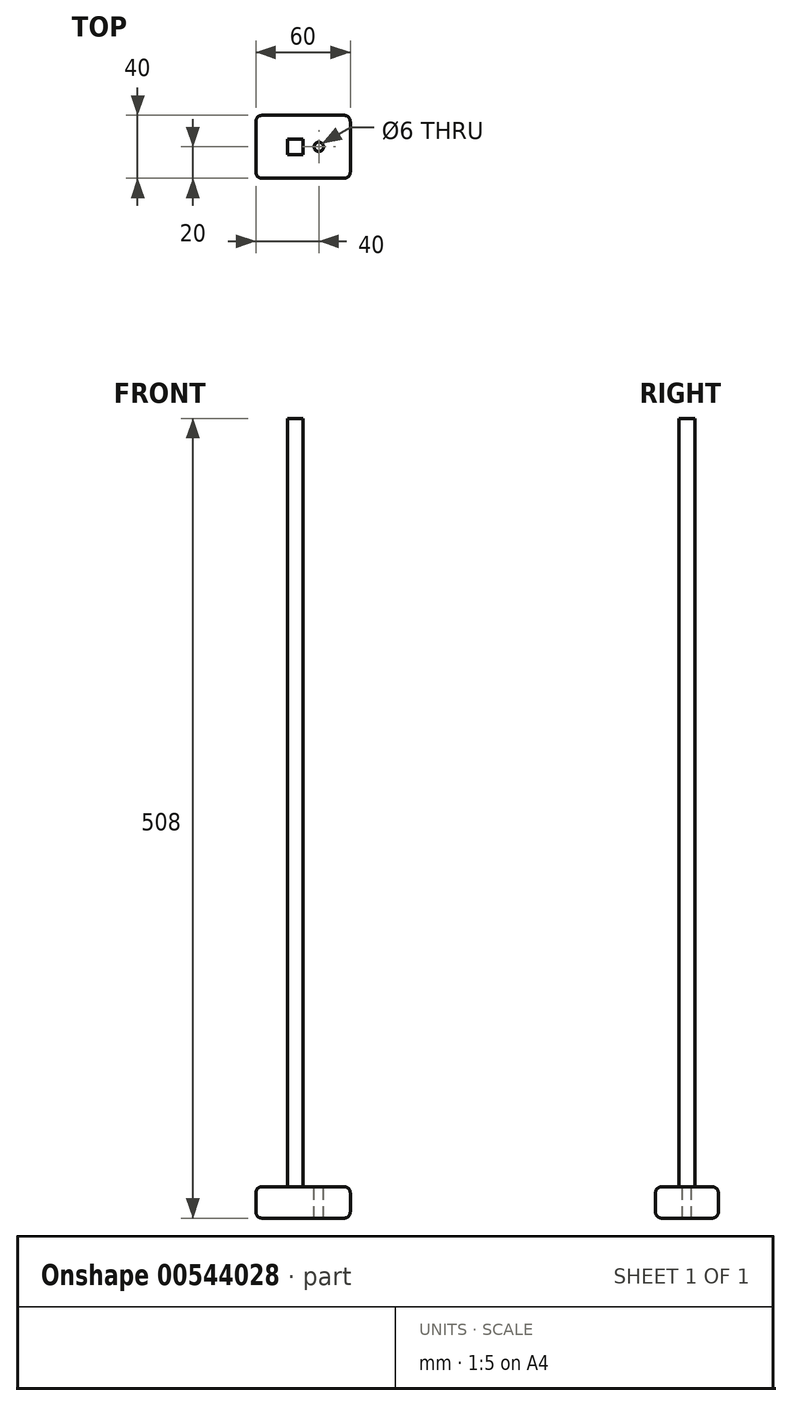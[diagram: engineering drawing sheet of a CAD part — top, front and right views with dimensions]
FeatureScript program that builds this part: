
annotation { "Feature Type Name" : "Feature", "Feature Type Description" : "" }
export const myFeature = defineFeature(function(context is Context, id is Id, definition is map)
    precondition{}
    {
        {
            var Q0;
            Q0=qCreatedBy(makeId("Front.planeOp"),FACE);
            var sketch = newSketch(context, id + "F0", { "sketchPlane" : qUnion([Q0])});
            skLineSegment(sketch, "E0.bottom", {"start": v(0, 0) * mm, "end": v(60, 0) * mm});
            skLineSegment(sketch, "E0.top", {"start": v(0, -20) * mm, "end": v(60, -20) * mm});
            skLineSegment(sketch, "E0.left", {"start": v(0, 0) * mm, "end": v(0, -20) * mm});
            skLineSegment(sketch, "E0.right", {"start": v(60, 0) * mm, "end": v(60, -20) * mm});
            skPoint(sketch, "E0.middle", {"position": v(30, -10) * mm});
            skSolve(sketch);
        }
        {
            var Q0;
            Q0=makeQuery(id+"F0.imprint","IMPRINT",FACE,{"disambiguationData":[TD([[makeQuery(id+"F0.imprint","IMPRINT",EDGE,{"derivedFrom":sQuery(id+"F0.wireOp",EDGE,"E0.bottom")}),-1.0]])]});
            extrude(context, id + "F1", {"entities" : qUnion([Q0]), "depth" : 40 * mm, "offsetDistance" : 25.4 * mm});
        }
        {
            var Q0;
            Q0=makeQuery(id+"F1.opExtrude","SWEPT_FACE",FACE,{"disambiguationData":[OSD([sQuery(id+"F0.wireOp",EDGE,"E0.bottom")])]});
            var sketch = newSketch(context, id + "F2", { "sketchPlane" : qUnion([Q0])});
            skCircle(sketch, "E1", {"center": v(40, -20) * mm, "radius": 10 * mm});
            skSolve(sketch);
        }
        {
            var Q0;
            Q0=makeQuery(id+"F1.opExtrude","CAP_EDGE",EDGE,{"disambiguationData":[OSD([sQuery(id+"F0.wireOp",EDGE,"E0.right")])],"isStart":true});
            var Q1;
            Q1=makeQuery(id+"F1.opExtrude","SWEPT_EDGE",EDGE,{"disambiguationData":[OSD([sQuery(id+"F0.wireOp",EDGE,"E0.top"),sQuery(id+"F0.wireOp",EDGE,"E0.left")])]});
            var Q2;
            Q2=makeQuery(id+"F1.opExtrude","CAP_EDGE",EDGE,{"disambiguationData":[OSD([sQuery(id+"F0.wireOp",EDGE,"E0.left")])],"isStart":true});
            var Q3;
            Q3=makeQuery(id+"F1.opExtrude","SWEPT_EDGE",EDGE,{"disambiguationData":[OSD([sQuery(id+"F0.wireOp",EDGE,"E0.bottom"),sQuery(id+"F0.wireOp",EDGE,"E0.left")])]});
            var Q4;
            Q4=makeQuery(id+"F1.opExtrude","CAP_EDGE",EDGE,{"disambiguationData":[OSD([sQuery(id+"F0.wireOp",EDGE,"E0.left")])],"isStart":false});
            var Q5;
            Q5=makeQuery(id+"F1.opExtrude","SWEPT_EDGE",EDGE,{"disambiguationData":[OSD([sQuery(id+"F0.wireOp",EDGE,"E0.top"),sQuery(id+"F0.wireOp",EDGE,"E0.right")])]});
            var Q6;
            Q6=makeQuery(id+"F1.opExtrude","CAP_EDGE",EDGE,{"disambiguationData":[OSD([sQuery(id+"F0.wireOp",EDGE,"E0.right")])],"isStart":false});
            var Q7;
            Q7=makeQuery(id+"F1.opExtrude","SWEPT_EDGE",EDGE,{"disambiguationData":[OSD([sQuery(id+"F0.wireOp",EDGE,"E0.bottom"),sQuery(id+"F0.wireOp",EDGE,"E0.right")])]});
            var Q8;
            Q8=makeQuery(id+"F1.opExtrude","CAP_EDGE",EDGE,{"disambiguationData":[OSD([sQuery(id+"F0.wireOp",EDGE,"E0.bottom")])],"isStart":false});
            var Q9;
            Q9=makeQuery(id+"F1.opExtrude","CAP_FACE",FACE,{"disambiguationData":[OSD([sQuery(id+"F0.wireOp",EDGE,"E0.bottom"),sQuery(id+"F0.wireOp",EDGE,"E0.top"),sQuery(id+"F0.wireOp",EDGE,"E0.left"),sQuery(id+"F0.wireOp",EDGE,"E0.right")])],"isStart":false});
            var Q10;
            Q10=makeQuery(id+"F1.opExtrude","CAP_EDGE",EDGE,{"disambiguationData":[OSD([sQuery(id+"F0.wireOp",EDGE,"E0.top")])],"isStart":true});
            var Q11;
            Q11=makeQuery(id+"F1.opExtrude","CAP_EDGE",EDGE,{"disambiguationData":[OSD([sQuery(id+"F0.wireOp",EDGE,"E0.bottom")])],"isStart":true});
            fillet(context, id + "F3", {"entities" : qUnion([Q0, Q1, Q2, Q3, Q4, Q5, Q6, Q7, Q8, Q9, Q10, Q11]), "radius" : 4 * mm, "tangentPropagation" : true, "allowEdgeOverflow" : false});
        }
        {
            var Q0;
            Q0=sQuery(id+"F2.wireOp",VERTEX,"E1.center");
            var Q1;
            Q1=makeQuery(id+"F1.opExtrude","SWEPT_BODY",BODY,{"disambiguationData":[OSD([sQuery(id+"F0.wireOp",EDGE,"E0.bottom"),sQuery(id+"F0.wireOp",EDGE,"E0.top"),sQuery(id+"F0.wireOp",EDGE,"E0.left"),sQuery(id+"F0.wireOp",EDGE,"E0.right")])]});
            hole(context, id + "F4", {"style" : HoleStyle.SIMPLE, "endStyle" : HoleEndStyle.THROUGH, "holeDiameter" : 6 * mm, "isTappedThrough" : true, "tappedDepth" : 12.7 * mm, "tapClearance" : 3, "locations" : qUnion([Q0]), "scope" : qUnion([Q1])});
        }
        {
            var Q0;
            Q0=makeQuery(id+"F1.opExtrude","SWEPT_FACE",FACE,{"disambiguationData":[OSD([sQuery(id+"F0.wireOp",EDGE,"E0.top")])]});
            var sketch = newSketch(context, id + "F5", { "sketchPlane" : qUnion([Q0])});
            skLineSegment(sketch, "E2.bottom", {"start": v(20, 25) * mm, "end": v(30, 25) * mm});
            skLineSegment(sketch, "E2.top", {"start": v(20, 15) * mm, "end": v(30, 15) * mm});
            skLineSegment(sketch, "E2.left", {"start": v(20, 25) * mm, "end": v(20, 15) * mm});
            skLineSegment(sketch, "E2.right", {"start": v(30, 25) * mm, "end": v(30, 15) * mm});
            skSolve(sketch);
        }
        {
            var Q0;
            Q0=makeQuery(id+"F5.imprint","IMPRINT",FACE,{"disambiguationData":[TD([[makeQuery(id+"F5.imprint","IMPRINT",EDGE,{"derivedFrom":sQuery(id+"F5.wireOp",EDGE,"E2.bottom")}),-1.0]])]});
            extrude(context, id + "F6", {"entities" : qUnion([Q0]), "operationType" : NewBodyOperationType.ADD, "oppositeDirection" : true, "depth" : 508 * mm, "offsetDistance" : 25.4 * mm});
        }
    });
